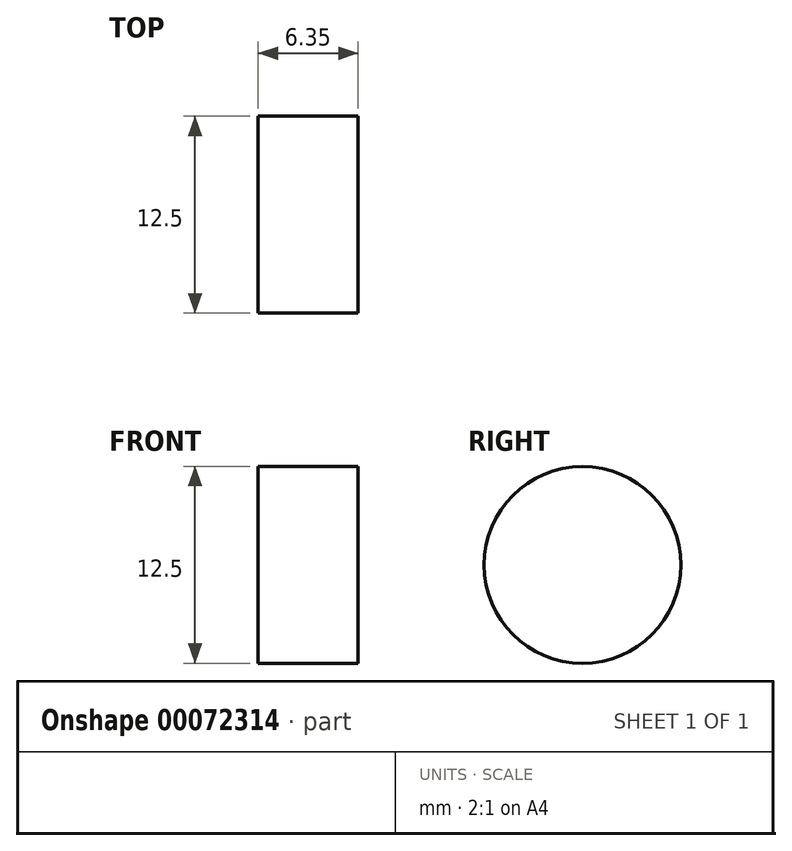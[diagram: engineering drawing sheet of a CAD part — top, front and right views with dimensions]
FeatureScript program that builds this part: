
annotation { "Feature Type Name" : "Feature", "Feature Type Description" : "" }
export const myFeature = defineFeature(function(context is Context, id is Id, definition is map)
    precondition{}
    {
        {
            var Q0;
            Q0=qCreatedBy(makeId("Front.planeOp"),FACE);
            var sketch = newSketch(context, id + "F0", { "sketchPlane" : qUnion([Q0])});
            skCircle(sketch, "E0", {"center": v(0, 0) * mm, "radius": 6.25 * mm});
            skSolve(sketch);
        }
        {
            var Q0;
            Q0 = qSketchRegion(id + "F0", true);
            extrude(context, id + "F1", {"entities" : qUnion([Q0]), "depth" : 6.35 * mm});
        }
        {
            var Q0;
            Q0=qCreatedBy(makeId("Right.planeOp"),FACE);
            var sketch = newSketch(context, id + "F2", { "sketchPlane" : qUnion([Q0])});
            skLineSegment(sketch, "E1", {"start": v(0, 36.87) * mm, "end": v(0, -33.1) * mm});
            skSolve(sketch);
        }
        {
            var Q0;
            Q0=makeQuery(id+"F1.opExtrude","SWEPT_BODY",BODY,{"disambiguationData":[OSD([sQuery(id+"F0.wireOp",EDGE,"E0")])]});
            var Q1;
            Q1=sQuery(id+"F2.wireOp",EDGE,"E1");
            transform(context, id + "F3", {"entities" : qUnion([Q0]), "transformType" : TransformType.ROTATION, "transformAxis" : qUnion([Q1]), "angle" : 90 * degree, "makeCopy" : false});
        }
    });
